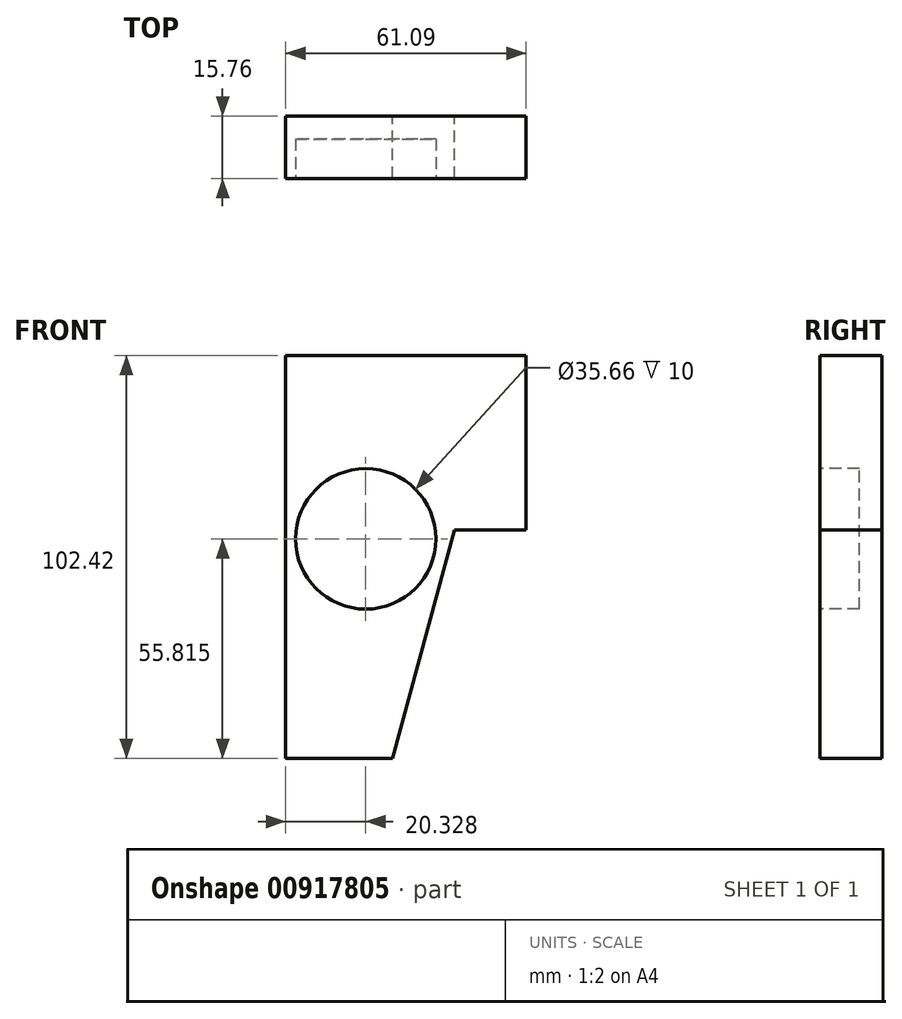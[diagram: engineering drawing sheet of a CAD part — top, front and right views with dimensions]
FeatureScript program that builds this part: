
annotation { "Feature Type Name" : "Feature", "Feature Type Description" : "" }
export const myFeature = defineFeature(function(context is Context, id is Id, definition is map)
    precondition{}
    {
        {
            var Q0;
            Q0=qCreatedBy(makeId("Front.planeOp"),FACE);
            var sketch = newSketch(context, id + "F0", { "sketchPlane" : qUnion([Q0])});
            skLineSegment(sketch, "E0", {"start": v(27.2, -28) * mm, "end": v(42.92, 30.09) * mm});
            skLineSegment(sketch, "E1", {"start": v(42.92, 30.09) * mm, "end": v(61.1, 30.09) * mm});
            skLineSegment(sketch, "E2", {"start": v(61.1, 30.09) * mm, "end": v(61.1, 74.42) * mm});
            skLineSegment(sketch, "E3", {"start": v(61.1, 74.42) * mm, "end": v(0, 74.42) * mm});
            skLineSegment(sketch, "E4", {"start": v(0, 74.42) * mm, "end": v(0, -28) * mm});
            skLineSegment(sketch, "E5", {"start": v(0, -28) * mm, "end": v(27.2, -28) * mm});
            skSolve(sketch);
        }
        {
            var Q0;
            Q0=makeQuery(id+"F0.imprint","IMPRINT",FACE,{"disambiguationData":[TD([[makeQuery(id+"F0.imprint","IMPRINT",EDGE,{"derivedFrom":sQuery(id+"F0.wireOp",EDGE,"E0")}),1.0]])]});
            extrude(context, id + "F1", {"entities" : qUnion([Q0]), "depth" : 15.76 * mm, "offsetDistance" : 25.4 * mm});
        }
        {
            var Q0;
            Q0=makeQuery(id+"F1.opExtrude","CAP_FACE",FACE,{"disambiguationData":[OSD([sQuery(id+"F0.wireOp",EDGE,"E0"),sQuery(id+"F0.wireOp",EDGE,"E1"),sQuery(id+"F0.wireOp",EDGE,"E2"),sQuery(id+"F0.wireOp",EDGE,"E3"),sQuery(id+"F0.wireOp",EDGE,"E4"),sQuery(id+"F0.wireOp",EDGE,"E5")])],"isStart":false});
            var sketch = newSketch(context, id + "F2", { "sketchPlane" : qUnion([Q0])});
            skCircle(sketch, "E6", {"center": v(20.33, 59.07) * mm, "radius": 2.08 * mm});
            skCircle(sketch, "E7", {"center": v(20.33, 27.82) * mm, "radius": 17.83 * mm});
            skSolve(sketch);
        }
        {
            var Q0;
            Q0=makeQuery(id+"F2.imprint","IMPRINT",FACE,{"disambiguationData":[TD([[makeQuery(id+"F2.imprint","IMPRINT",EDGE,{"derivedFrom":sQuery(id+"F2.wireOp",EDGE,"E7")}),1.0]])]});
            var Q1;
            Q1=sQuery(id+"F2.wireOp",EDGE,"E7");
            extrude(context, id + "F3", {"entities" : qUnion([Q0]), "operationType" : NewBodyOperationType.REMOVE, "surfaceEntities" : qUnion([Q1]), "oppositeDirection" : true, "depth" : 10 * mm, "offsetDistance" : 25.4 * mm});
        }
    });
